# Revit family: Winmaster_Lodret Bundsamling med Isoleringsbjælke_type 1 (Winmaster Greenboard)
name_source: partatom
category: Detail Items
units: mm (PartAtom-declared; Revit-internal decimal feet)

## family parameters
Rotate with component = No
Section Shape = Not Defined
Shared = Yes

## types (1)
- Type 1
    Anvendelse = Beton, mursten og gasbeton
    Brandklasse af pladefalsen = Brandklasse A1
    Bredder af bærebeslag = 9mm, 12mm, 15mm, 18mm, 21mm, 24mm, 27mm
    Bæreevne af Isoleringsbjælke = Punktbelastning 100 kg,

IKKE BÆRENDE
    Bæreevne af bærebeslag = Optil 100 kg pr. beslag
    Description = Bundsamling m. bærebeslag og isoleringsbjælke
    Funktion = Understøtter vinduet i forbindelse med montage
    Galvaniseret stål = Klasse 2-3
    Isoleringsbjælke (mål) = 50 x Justerbar i højden mm
    Isoleringsbjælke m. plade = No
    Isoleringsbjælke m. trykbeslag = Yes
    Linjetab af Isoleringsbjælke = 0,033 W/mK
    Linjetab af pladefalsen = 0,33 W/mk
    Manufacturer = WINMASTER
    Material_Bærebeslag = Rustfrit stål (tilkøb klasse 5)
    Material_Isolering = PU Skum
    Material_Isoleringsbjælke = Trykfast polystyren
    Material_Mørtel = Limmørtel
    Material_Pladefalsen = Lysningsplade
    Tykkelse af bærebeslag = 2 mm
    URL = https://winmaster.dk
    Udført af = Tegnestuen Tankestregen
    WINMASTER_Bærebeslag = https://winmaster.dk
    WINMASTER_Isoleringsbjælke = https://winmaster.dk
    WINMASTER_Pladefalsen = https://winmaster.dk
    WINMASTER_URL = https://winmaster.dk

## geometry (parser evidence)
native form markers: Sweep x33
no freeform markers — native parametric forms only
